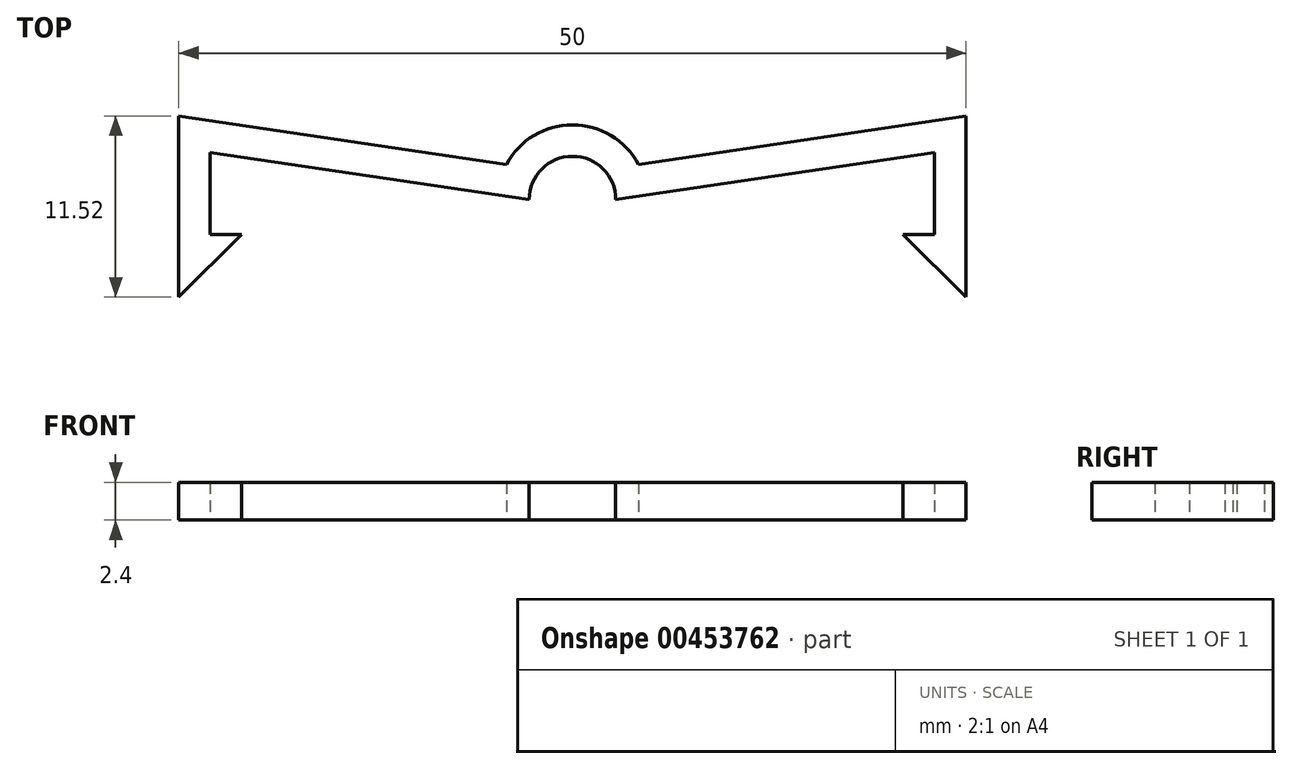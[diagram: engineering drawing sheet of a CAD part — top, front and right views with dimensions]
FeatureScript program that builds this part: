
annotation { "Feature Type Name" : "Feature", "Feature Type Description" : "" }
export const myFeature = defineFeature(function(context is Context, id is Id, definition is map)
    precondition{}
    {
        {
            var Q0;
            Q0=qCreatedBy(makeId("Top.planeOp"),FACE);
            var sketch = newSketch(context, id + "F0", { "sketchPlane" : qUnion([Q0])});
            skLineSegment(sketch, "E0", {"start": v(25, 7.52) * mm, "end": v(25, -4) * mm});
            skLineSegment(sketch, "E1", {"start": v(25, -4) * mm, "end": v(21, 0) * mm});
            skLineSegment(sketch, "E2", {"start": v(21, 0) * mm, "end": v(23, 0) * mm});
            skLineSegment(sketch, "E3", {"start": v(23, 0) * mm, "end": v(23, 5.2) * mm});
            skLineSegment(sketch, "E4.MirrorCS", {"start": v(-23, 0) * mm, "end": v(-23, 5.2) * mm});
            skLineSegment(sketch, "E5.MirrorCS", {"start": v(-21, 0) * mm, "end": v(-23, 0) * mm});
            skLineSegment(sketch, "E6.MirrorCS", {"start": v(-25, -4) * mm, "end": v(-21, 0) * mm});
            skLineSegment(sketch, "E7.MirrorCS", {"start": v(-25, 7.52) * mm, "end": v(-25, -4) * mm});
            skLineSegment(sketch, "E8", {"start": v(23, 5.2) * mm, "end": v(2.75, 2.2) * mm});
            skArc(sketch, "E9", {"start": v(2.75, 2.2) * mm, "mid": v(0, 4.95) * mm, "end": v(-2.75, 2.2) * mm});
            skLineSegment(sketch, "E10", {"start": v(25, 7.52) * mm, "end": v(4.2, 4.44) * mm});
            skArc(sketch, "E11", {"start": v(4.2, 4.44) * mm, "mid": v(0, 6.95) * mm, "end": v(-4.2, 4.44) * mm});
            skLineSegment(sketch, "E12.MirrorCS", {"start": v(-25, 7.52) * mm, "end": v(-4.2, 4.44) * mm});
            skLineSegment(sketch, "E13.MirrorCS", {"start": v(-23, 5.2) * mm, "end": v(-2.75, 2.2) * mm});
            skSolve(sketch);
        }
        {
            var Q0;
            Q0 = qSketchRegion(id + "F0", true);
            extrude(context, id + "F1", {"entities" : qUnion([Q0]), "endBound" : BoundingType.SYMMETRIC, "depth" : 2.4 * mm});
        }
    });
